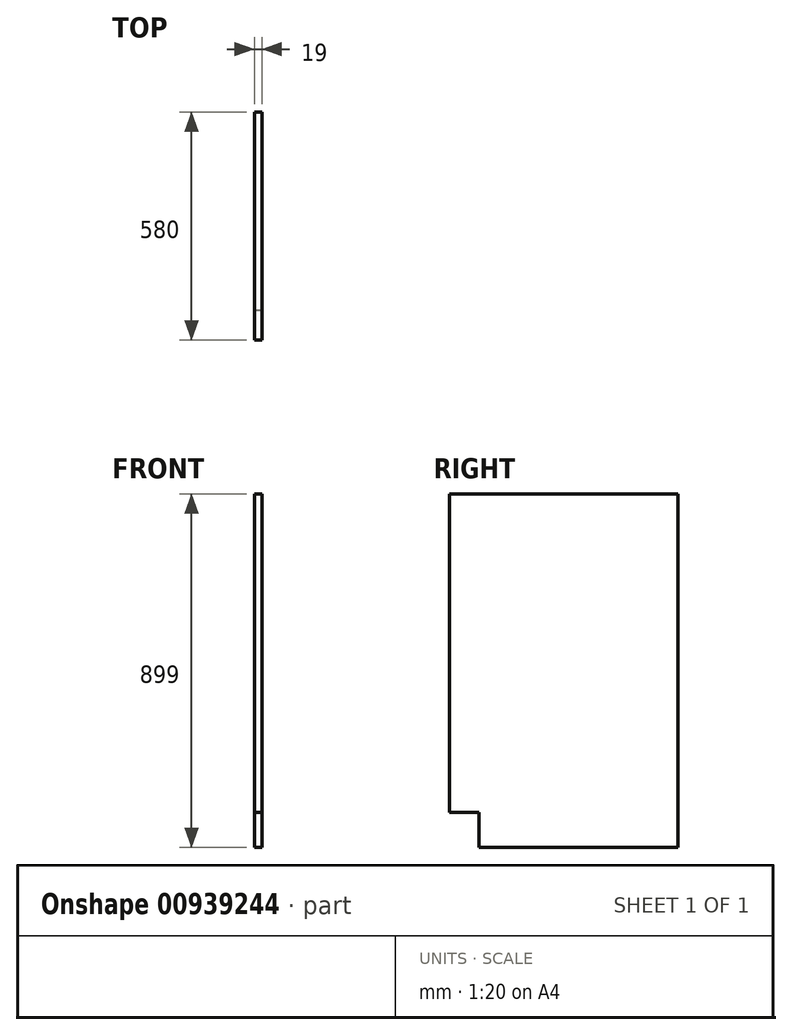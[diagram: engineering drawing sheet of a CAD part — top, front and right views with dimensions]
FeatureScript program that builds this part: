
annotation { "Feature Type Name" : "Feature", "Feature Type Description" : "" }
export const myFeature = defineFeature(function(context is Context, id is Id, definition is map)
    precondition{}
    {
        {
            var Q0;
            Q0=qCreatedBy(makeId("Right.planeOp"),FACE);
            var sketch = newSketch(context, id + "F0", { "sketchPlane" : qUnion([Q0])});
            skLineSegment(sketch, "E0.bottom", {"start": v(0, 0) * mm, "end": v(-505, 0) * mm});
            skLineSegment(sketch, "E0.top", {"start": v(0, 899) * mm, "end": v(-580, 899) * mm});
            skLineSegment(sketch, "E0.left", {"start": v(0, 0) * mm, "end": v(0, 899) * mm});
            skLineSegment(sketch, "E0.right", {"start": v(-580, 90) * mm, "end": v(-580, 899) * mm});
            skLineSegment(sketch, "E1", {"start": v(-505, 0) * mm, "end": v(-505, 90) * mm});
            skLineSegment(sketch, "E2", {"start": v(-505, 90) * mm, "end": v(-580, 90) * mm});
            skSolve(sketch);
        }
        {
            var Q0;
            Q0=qSketchRegion(id+"F0",true);
            extrude(context, id + "F1", {"entities" : qUnion([Q0]), "depth" : 19 * mm, "offsetDistance" : 25 * mm});
        }
    });
